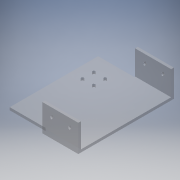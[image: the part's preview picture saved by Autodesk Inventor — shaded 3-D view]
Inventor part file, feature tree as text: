
AUTODESK INVENTOR PART (.ipt)
format: ipt  version: 2016 (Build 200138000, 138)  size: 138,752 bytes
history: native  units: in
note: dims shown in document units (in); Inventor stores cm internally (conversion verified against a paired STEP export)
features: sketch x6, extrude x4, reference x4, hole x2
ambient origin geometry x8: Origin, YZ Plane, XZ Plane, XY Plane, X Axis, Y Axis, Z Axis, Center Point
bodies: Solid1 (feature_tree)
feature tree (16):
  extrude  "Extrusion1"  Depth=5.3in
  extrude  "Extrusion2"  Depth=5.0in
  extrude  "Extrusion3"  Depth=2.0in
  extrude  "Extrusion4"  Depth=0.2in TaperAngle=0.0deg
  hole  "Hole1"  [1 undecoded]
  hole  "Hole2"  [1 undecoded]
  sketch  "Sketch1"  dims[d0=4.0in d1=5.3in]
  sketch  "Sketch3"  dims[d2=1.5in d3=0.0in d4=5.0in]
  sketch  "Sketch4"  dims[d5=1.35in d6=0.0in d7=2.0in]
  sketch  "Sketch5"  dims[d8=0.2in d9=0.0in d10=0.2in d11=0.0in]
  sketch  "Sketch6"  dims[d12=0.5in d13=0.5in]
  sketch  "Sketch8"  dims[d14=0.5in d15=0.1457in d16=0.75in d17=0.375in d18=0.25in d19=0.5635in d20=1.0in d21=0.8108in d22=0.1457in d23=0.75in d24=0.375in d25=0.25in d26=0.5635in d27=1.0in d28=0.8108in]
  reference  "Reference9"
  reference  "Reference10"
  reference  "Reference11"
  reference  "Reference12"
note: 2 required parameter values undecoded (feature->parameter linkage not recoverable at this tier; creation-order binding heuristic only, values carry confidence <= 0.55)
